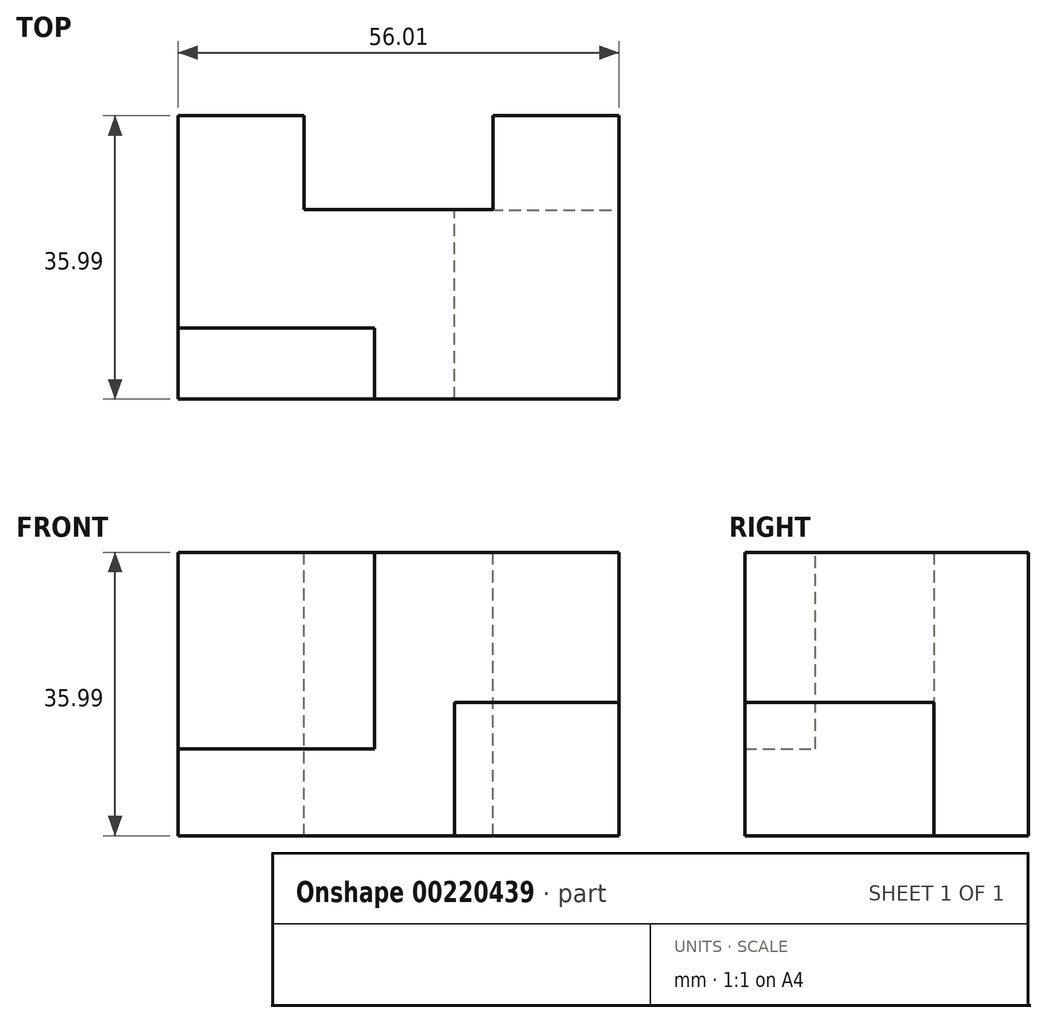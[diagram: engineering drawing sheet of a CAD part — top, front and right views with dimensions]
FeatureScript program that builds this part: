
annotation { "Feature Type Name" : "Feature", "Feature Type Description" : "" }
export const myFeature = defineFeature(function(context is Context, id is Id, definition is map)
    precondition{}
    {
        {
            var Q0;
            Q0=qCreatedBy(makeId("Top.planeOp"),FACE);
            var sketch = newSketch(context, id + "F0", { "sketchPlane" : qUnion([Q0])});
            skLineSegment(sketch, "E0.bottom", {"start": v(0, 0) * mm, "end": v(56, 0) * mm});
            skLineSegment(sketch, "E0.top", {"start": v(0, 36) * mm, "end": v(16, 36) * mm});
            skLineSegment(sketch, "E0.left", {"start": v(0, 0) * mm, "end": v(0, 36) * mm});
            skLineSegment(sketch, "E0.right", {"start": v(56, 0) * mm, "end": v(56, 36) * mm});
            skLineSegment(sketch, "E1.0", {"start": v(16, 24.05) * mm, "end": v(16, 36) * mm});
            skLineSegment(sketch, "E2.0", {"start": v(40, 24.05) * mm, "end": v(40, 36) * mm});
            skLineSegment(sketch, "E3.0", {"start": v(16, 24.05) * mm, "end": v(40, 24.05) * mm});
            skLineSegment(sketch, "E4.trimOffspring", {"start": v(40, 36) * mm, "end": v(56, 36) * mm});
            skSolve(sketch);
        }
        {
            var Q0;
            Q0=makeQuery(id+"F0.imprint","IMPRINT",FACE,{"disambiguationData":[TD([[makeQuery(id+"F0.imprint","IMPRINT",EDGE,{"derivedFrom":sQuery(id+"F0.wireOp",EDGE,"E0.bottom")}),1.0]])]});
            extrude(context, id + "F1", {"entities" : qUnion([Q0]), "oppositeDirection" : true, "depth" : 36 * mm});
        }
        {
            var Q0;
            Q0=makeQuery(id+"F1.opExtrude","SWEPT_FACE",FACE,{"disambiguationData":[OSD([sQuery(id+"F0.wireOp",EDGE,"E0.right")])]});
            var sketch = newSketch(context, id + "F2", { "sketchPlane" : qUnion([Q0])});
            skLineSegment(sketch, "E5.bottom", {"start": v(0, -19.05) * mm, "end": v(24, -19.05) * mm});
            skLineSegment(sketch, "E5.top", {"start": v(0, -36) * mm, "end": v(24, -36) * mm});
            skLineSegment(sketch, "E5.left", {"start": v(0, -19.05) * mm, "end": v(0, -36) * mm});
            skLineSegment(sketch, "E5.right", {"start": v(24, -19.05) * mm, "end": v(24, -36) * mm});
            skSolve(sketch);
        }
        {
            var Q0;
            Q0=makeQuery(id+"F2.imprint","IMPRINT",FACE,{"disambiguationData":[TD([[makeQuery(id+"F2.imprint","IMPRINT",EDGE,{"derivedFrom":sQuery(id+"F2.wireOp",EDGE,"E5.bottom")}),-1.0]])]});
            extrude(context, id + "F3", {"entities" : qUnion([Q0]), "operationType" : NewBodyOperationType.REMOVE, "oppositeDirection" : true, "depth" : 20.85 * mm});
        }
        {
            var Q0;
            Q0=makeQuery(id+"F1.opExtrude","CAP_FACE",FACE,{"disambiguationData":[OSD([sQuery(id+"F0.wireOp",EDGE,"E0.bottom"),sQuery(id+"F0.wireOp",EDGE,"E0.top"),sQuery(id+"F0.wireOp",EDGE,"E0.left"),sQuery(id+"F0.wireOp",EDGE,"E0.right"),sQuery(id+"F0.wireOp",EDGE,"E1.0"),sQuery(id+"F0.wireOp",EDGE,"E2.0"),sQuery(id+"F0.wireOp",EDGE,"E3.0"),sQuery(id+"F0.wireOp",EDGE,"E4.trimOffspring")])],"isStart":true});
            var sketch = newSketch(context, id + "F4", { "sketchPlane" : qUnion([Q0])});
            skLineSegment(sketch, "E6.bottom", {"start": v(0, 9) * mm, "end": v(24.97, 9) * mm});
            skLineSegment(sketch, "E6.top", {"start": v(0, 0) * mm, "end": v(24.97, 0) * mm});
            skLineSegment(sketch, "E6.left", {"start": v(0, 9) * mm, "end": v(0, 0) * mm});
            skLineSegment(sketch, "E6.right", {"start": v(24.97, 9) * mm, "end": v(24.97, 0) * mm});
            skSolve(sketch);
        }
        {
            var Q0;
            Q0=makeQuery(id+"F4.imprint","IMPRINT",FACE,{"disambiguationData":[TD([[makeQuery(id+"F4.imprint","IMPRINT",EDGE,{"derivedFrom":sQuery(id+"F4.wireOp",EDGE,"E6.bottom")}),-1.0]])]});
            extrude(context, id + "F5", {"entities" : qUnion([Q0]), "operationType" : NewBodyOperationType.REMOVE, "oppositeDirection" : true, "depth" : 24.94 * mm});
        }
    });
